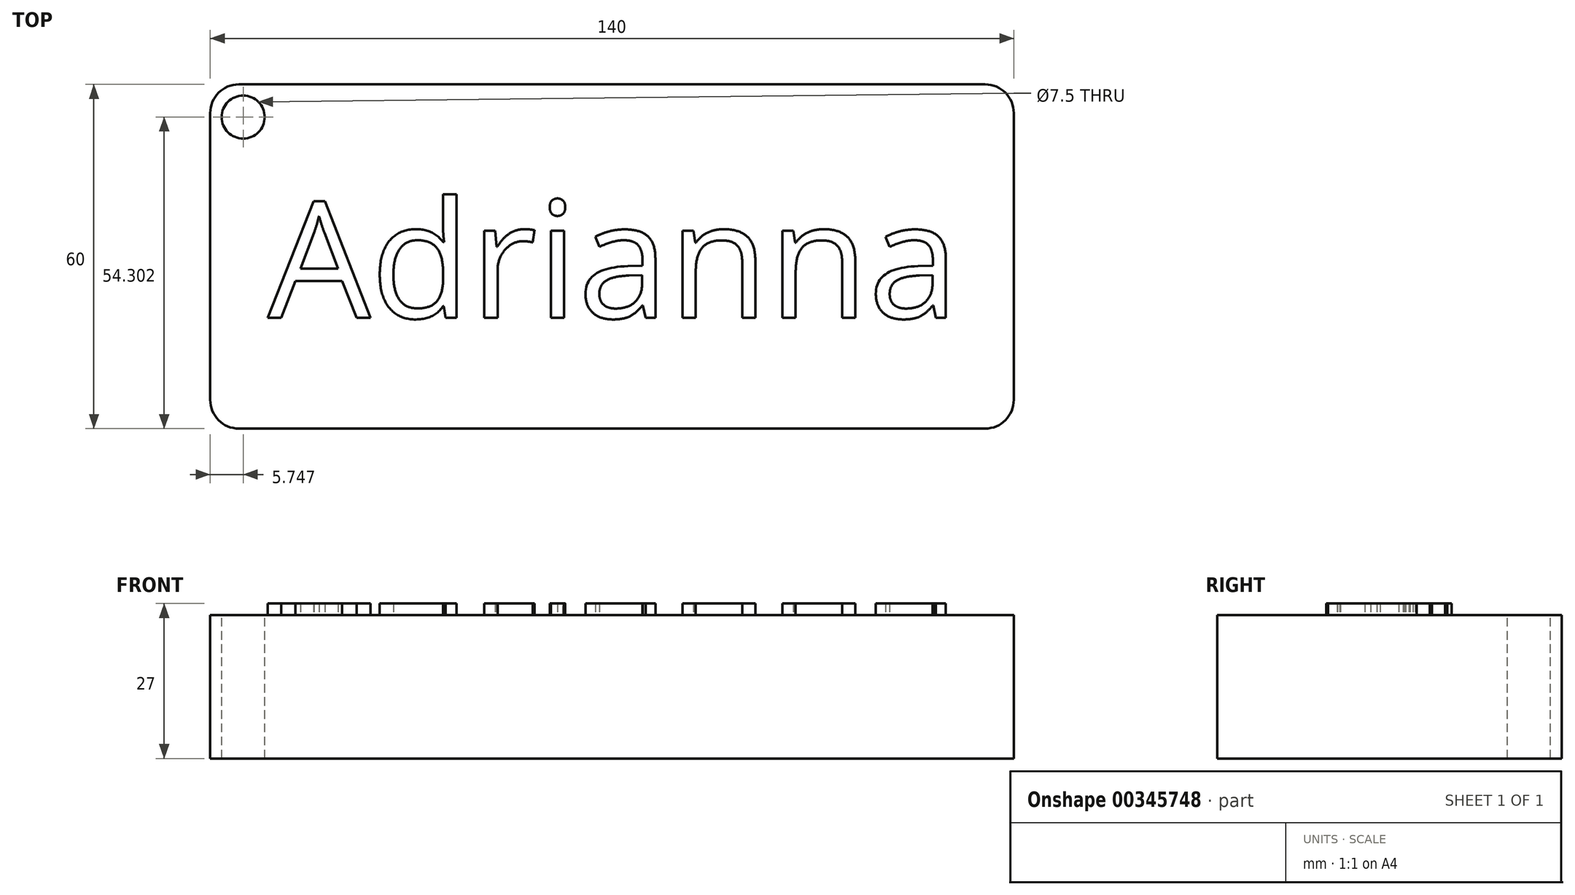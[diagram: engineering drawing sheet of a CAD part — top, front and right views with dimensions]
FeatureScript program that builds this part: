
annotation { "Feature Type Name" : "Feature", "Feature Type Description" : "" }
export const myFeature = defineFeature(function(context is Context, id is Id, definition is map)
    precondition{}
    {
        {
            var Q0;
            Q0=qCreatedBy(makeId("Top.planeOp"),FACE);
            var sketch = newSketch(context, id + "F0", { "sketchPlane" : qUnion([Q0])});
            skLineSegment(sketch, "E0.bottom", {"start": v(-70, 30) * mm, "end": v(70, 30) * mm});
            skLineSegment(sketch, "E0.top", {"start": v(-70, -30) * mm, "end": v(70, -30) * mm});
            skLineSegment(sketch, "E0.left", {"start": v(-70, 30) * mm, "end": v(-70, -30) * mm});
            skLineSegment(sketch, "E0.right", {"start": v(70, 30) * mm, "end": v(70, -30) * mm});
            skSolve(sketch);
        }
        {
            var Q0;
            Q0=makeQuery(id+"F0.imprint","IMPRINT",FACE,{"disambiguationData":[TD([[makeQuery(id+"F0.imprint","IMPRINT",EDGE,{"derivedFrom":sQuery(id+"F0.wireOp",EDGE,"E0.bottom")}),-1.0]])]});
            extrude(context, id + "F1", {"entities" : qUnion([Q0]), "depth" : 25 * mm});
        }
        {
            var Q0;
            Q0=makeQuery(id+"F1.opExtrude","CAP_FACE",FACE,{"disambiguationData":[OSD([sQuery(id+"F0.wireOp",EDGE,"E0.bottom"),sQuery(id+"F0.wireOp",EDGE,"E0.top"),sQuery(id+"F0.wireOp",EDGE,"E0.left"),sQuery(id+"F0.wireOp",EDGE,"E0.right")])],"isStart":false});
            var sketch = newSketch(context, id + "F2", { "sketchPlane" : qUnion([Q0])});
            skText(sketch, "E1", { "text": "Adrianna", "fontName": "OpenSans-Regular.ttf"});
            const initialGuessF2  = {"E1": [-0.06, -0.0107, 1, 0, 0.02042]};
            skSetInitialGuess(sketch, initialGuessF2);
            skSolve(sketch);
        }
        {
            var Q0;
            Q0 = qSketchRegion(id + "F2", true);
            extrude(context, id + "F3", {"entities" : qUnion([Q0]), "operationType" : NewBodyOperationType.ADD, "depth" : 2 * mm});
        }
        {
            var Q0;
            {var subQ0=sQuery(id+"F0.wireOp",EDGE,"E0.top");var subQ1=sQuery(id+"F0.wireOp",EDGE,"E0.right");var subQ2=sQuery(id+"F0.wireOp",EDGE,"E0.bottom");var subQ3=sQuery(id+"F0.wireOp",EDGE,"E0.left");Q0=makeQuery(id+"F3.boolean.opBoolean","SPLIT",FACE,{"disambiguationData":[TD([makeQuery(id+"F1.opExtrude","SWEPT_FACE",FACE,{"disambiguationData":[OSD([subQ2])]})])],"derivedFrom":makeQuery(id+"F1.opExtrude","CAP_FACE",FACE,{"disambiguationData":[OSD([subQ2,subQ0,subQ3,subQ1])],"isStart":false})});}
            var sketch = newSketch(context, id + "F4", { "sketchPlane" : qUnion([Q0])});
            skCircle(sketch, "E2", {"center": v(-64.25, 24.3) * mm, "radius": 3.75 * mm});
            skSolve(sketch);
        }
        {
            var Q0;
            Q0=makeQuery(id+"F4.imprint","IMPRINT",FACE,{"disambiguationData":[TD([[makeQuery(id+"F4.imprint","IMPRINT",EDGE,{"derivedFrom":sQuery(id+"F4.wireOp",EDGE,"E2")}),1.0]])]});
            extrude(context, id + "F5", {"entities" : qUnion([Q0]), "operationType" : NewBodyOperationType.REMOVE, "oppositeDirection" : true, "depth" : 25 * mm});
        }
        {
            var Q0;
            Q0=makeQuery(id+"F1.opExtrude","SWEPT_EDGE",EDGE,{"disambiguationData":[OSD([sQuery(id+"F0.wireOp",EDGE,"E0.top"),sQuery(id+"F0.wireOp",EDGE,"E0.right")])]});
            var Q1;
            Q1=makeQuery(id+"F1.opExtrude","SWEPT_EDGE",EDGE,{"disambiguationData":[OSD([sQuery(id+"F0.wireOp",EDGE,"E0.top"),sQuery(id+"F0.wireOp",EDGE,"E0.left")])]});
            var Q2;
            Q2=makeQuery(id+"F1.opExtrude","SWEPT_EDGE",EDGE,{"disambiguationData":[OSD([sQuery(id+"F0.wireOp",EDGE,"E0.bottom"),sQuery(id+"F0.wireOp",EDGE,"E0.right")])]});
            var Q3;
            Q3=makeQuery(id+"F1.opExtrude","SWEPT_EDGE",EDGE,{"disambiguationData":[OSD([sQuery(id+"F0.wireOp",EDGE,"E0.bottom"),sQuery(id+"F0.wireOp",EDGE,"E0.left")])]});
            fillet(context, id + "F6", {"entities" : qUnion([Q0, Q1, Q2, Q3]), "radius" : 5 * mm, "tangentPropagation" : true, "allowEdgeOverflow" : false});
        }
    });
